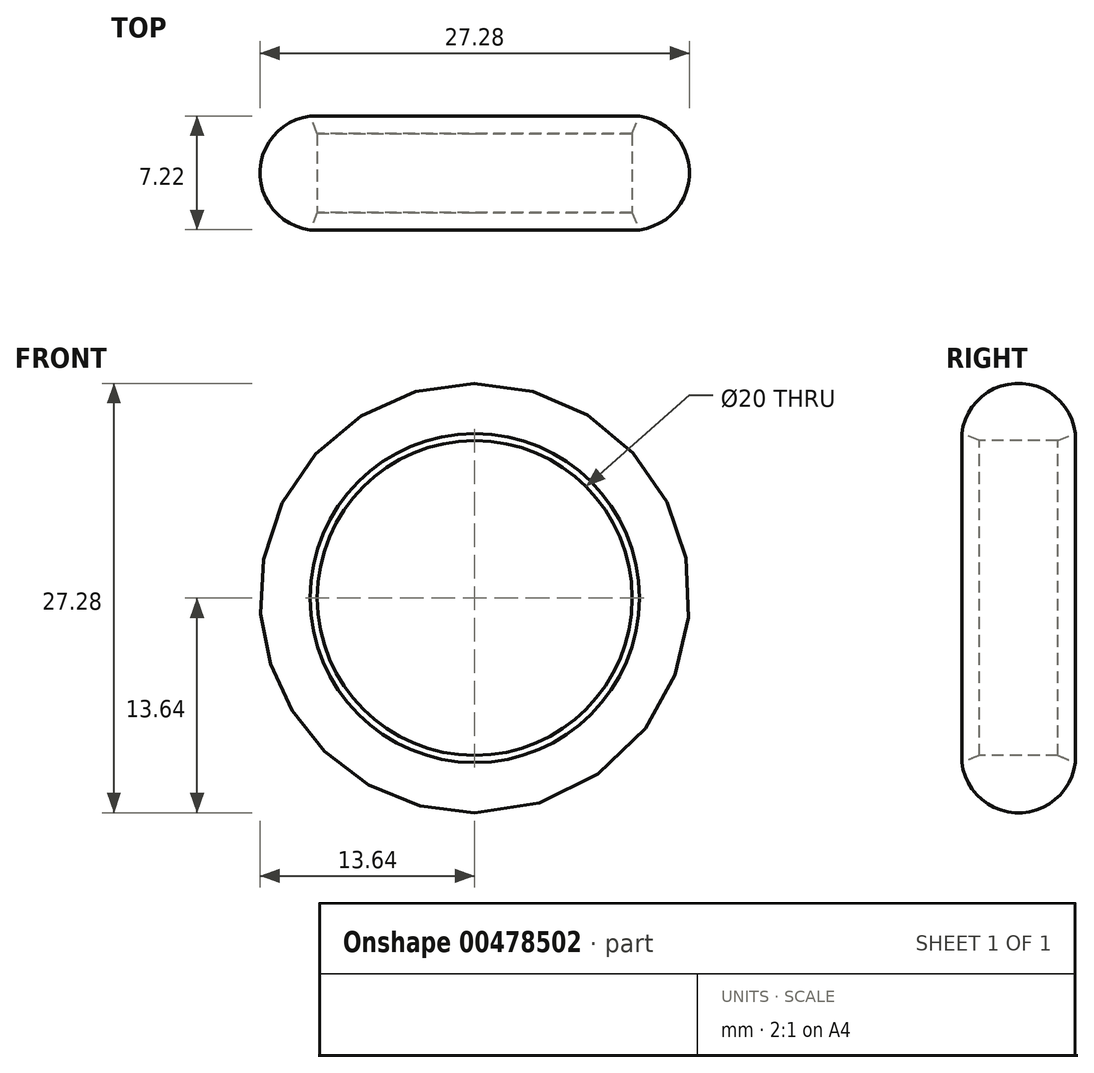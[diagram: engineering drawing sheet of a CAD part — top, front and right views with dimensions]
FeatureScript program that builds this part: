
annotation { "Feature Type Name" : "Feature", "Feature Type Description" : "" }
export const myFeature = defineFeature(function(context is Context, id is Id, definition is map)
    precondition{}
    {
        {
            var Q0;
            Q0=qCreatedBy(makeId("Top.planeOp"),FACE);
            var sketch = newSketch(context, id + "F0", { "sketchPlane" : qUnion([Q0])});
            skLineSegment(sketch, "E0", {"start": v(0, -1.46) * mm, "end": v(0, 2.74) * mm, "construction": true});
            skSolve(sketch);
        }
        {
            var Q0;
            Q0=qCreatedBy(makeId("Top.planeOp"),FACE);
            var sketch = newSketch(context, id + "F1", { "sketchPlane" : qUnion([Q0])});
            skLineSegment(sketch, "E1.bottom", {"start": v(10, 0) * mm, "end": v(10.45, -1.11) * mm});
            skLineSegment(sketch, "E1.top", {"start": v(10, 5) * mm, "end": v(10.45, 6.11) * mm});
            skLineSegment(sketch, "E1.left", {"start": v(10, 0) * mm, "end": v(10, 5) * mm});
            skArc(sketch, "E2", {"start": v(10.45, -1.11) * mm, "mid": v(13.64, 2.5) * mm, "end": v(10.45, 6.11) * mm});
            skSolve(sketch);
        }
        {
            var Q0;
            Q0=makeQuery(id+"F1.imprint","IMPRINT",FACE,{"disambiguationData":[TD([[makeQuery(id+"F1.imprint","IMPRINT",EDGE,{"derivedFrom":sQuery(id+"F1.wireOp",EDGE,"E1.bottom")}),1.0]])]});
            var Q1;
            Q1=sQuery(id+"F0.wireOp",EDGE,"E0");
            revolve(context, id + "F2", {"entities" : qUnion([Q0]), "axis" : qUnion([Q1]), "revolveType" : RevolveType.FULL});
        }
    });
